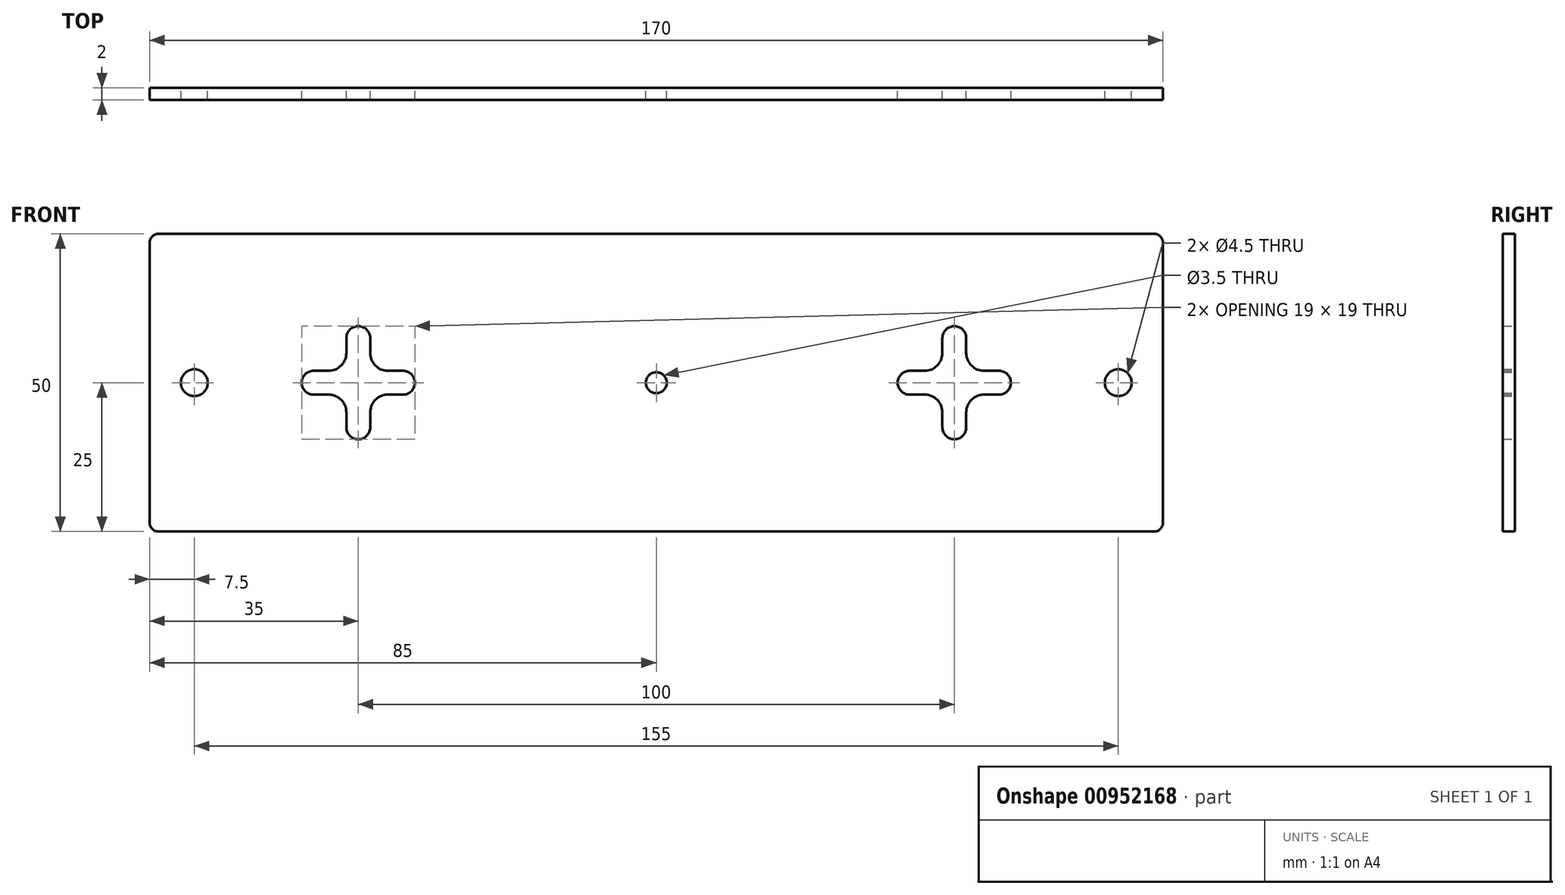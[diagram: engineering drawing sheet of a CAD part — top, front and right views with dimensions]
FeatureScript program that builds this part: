
annotation { "Feature Type Name" : "Feature", "Feature Type Description" : "" }
export const myFeature = defineFeature(function(context is Context, id is Id, definition is map)
    precondition{}
    {
        {
            var Q0;
            Q0=qCreatedBy(makeId("Front.planeOp"),FACE);
            var sketch = newSketch(context, id + "F0", { "sketchPlane" : qUnion([Q0])});
            skLineSegment(sketch, "E0.bottom", {"start": v(0, 0) * mm, "end": v(170, 0) * mm});
            skLineSegment(sketch, "E0.top", {"start": v(0, 50) * mm, "end": v(170, 50) * mm});
            skLineSegment(sketch, "E0.left", {"start": v(0, 0) * mm, "end": v(0, 50) * mm});
            skLineSegment(sketch, "E0.right", {"start": v(170, 0) * mm, "end": v(170, 50) * mm});
            skCircle(sketch, "E1", {"center": v(7.5, 25) * mm, "radius": 2.25 * mm});
            skCircle(sketch, "E2", {"center": v(162.5, 25) * mm, "radius": 2.25 * mm});
            skCircle(sketch, "E3", {"center": v(85, 25) * mm, "radius": 1.75 * mm});
            skLineSegment(sketch, "E4", {"start": v(35, 32.5) * mm, "end": v(35, 17.5) * mm});
            skLineSegment(sketch, "E5", {"start": v(27.5, 25) * mm, "end": v(42.5, 25) * mm});
            skArc(sketch, "E6.0.startCap", {"start": v(33, 32.5) * mm, "mid": v(35, 34.5) * mm, "end": v(37, 32.5) * mm});
            skArc(sketch, "E6.0.endCap", {"start": v(37, 17.5) * mm, "mid": v(35, 15.5) * mm, "end": v(33, 17.5) * mm});
            skLineSegment(sketch, "E6.0.left", {"start": v(37, 32.5) * mm, "end": v(37, 17.5) * mm});
            skLineSegment(sketch, "E6.0.right", {"start": v(33, 32.5) * mm, "end": v(33, 17.5) * mm});
            skArc(sketch, "E6.1.startCap", {"start": v(27.5, 23) * mm, "mid": v(25.5, 25) * mm, "end": v(27.5, 27) * mm});
            skArc(sketch, "E6.1.endCap", {"start": v(42.5, 27) * mm, "mid": v(44.5, 25) * mm, "end": v(42.5, 23) * mm});
            skLineSegment(sketch, "E6.1.left", {"start": v(27.5, 27) * mm, "end": v(42.5, 27) * mm});
            skLineSegment(sketch, "E6.1.right", {"start": v(27.5, 23) * mm, "end": v(42.5, 23) * mm});
            skLineSegment(sketch, "E7.1.0.0", {"start": v(127.5, 27) * mm, "end": v(142.5, 27) * mm});
            skLineSegment(sketch, "E7.1.0.1", {"start": v(135, 32.5) * mm, "end": v(135, 17.5) * mm});
            skLineSegment(sketch, "E7.1.0.2", {"start": v(133, 32.5) * mm, "end": v(133, 17.5) * mm});
            skLineSegment(sketch, "E7.1.0.3", {"start": v(137, 32.5) * mm, "end": v(137, 17.5) * mm});
            skArc(sketch, "E7.1.0.4", {"start": v(137, 17.5) * mm, "mid": v(135, 15.5) * mm, "end": v(133, 17.5) * mm});
            skArc(sketch, "E7.1.0.5", {"start": v(142.5, 27) * mm, "mid": v(144.5, 25) * mm, "end": v(142.5, 23) * mm});
            skLineSegment(sketch, "E7.1.0.6", {"start": v(127.5, 23) * mm, "end": v(142.5, 23) * mm});
            skArc(sketch, "E7.1.0.7", {"start": v(133, 32.5) * mm, "mid": v(135, 34.5) * mm, "end": v(137, 32.5) * mm});
            skArc(sketch, "E7.1.0.8", {"start": v(127.5, 23) * mm, "mid": v(125.5, 25) * mm, "end": v(127.5, 27) * mm});
            skLineSegment(sketch, "E7.1.0.9", {"start": v(127.5, 25) * mm, "end": v(142.5, 25) * mm});
            skLineSegment(sketch, "E7.direction1", {"start": v(33, 17.5) * mm, "end": v(133, 17.5) * mm, "construction": true});
            skSolve(sketch);
        }
        {
            var Q0;
            {var subQ1=sQuery(id+"F0.wireOp",EDGE,"E0.top");Q0=makeQuery(id+"F0.imprint","IMPRINT",FACE,{"disambiguationData":[TD([[makeQuery(id+"F0.imprint","IMPRINT",EDGE,{"derivedFrom":subQ1}),-1.0]])]});}
            var Q1;
            {var subQ8=sQuery(id+"F0.wireOp",EDGE,"2fdba3b7-9a52-4864-9b49-22906f5ad9b7.0");Q1=makeQuery(id+"F0.imprint","IMPRINT",FACE,{"disambiguationData":[TD([[makeQuery(id+"F0.imprint","IMPRINT",EDGE,{"derivedFrom":subQ8}),-1.0]])]});}
            var Q2;
            {var subQ5=sQuery(id+"F0.wireOp",EDGE,"64e2a2b8-9ee0-4563-ae59-12d8a678591b.0");Q2=makeQuery(id+"F0.imprint","IMPRINT",FACE,{"disambiguationData":[TD([[makeQuery(id+"F0.imprint","IMPRINT",EDGE,{"derivedFrom":subQ5}),1.0]])]});}
            var Q3;
            {var subQ1=sQuery(id+"F0.wireOp",EDGE,"E0.bottom");Q3=makeQuery(id+"F0.imprint","IMPRINT",FACE,{"disambiguationData":[TD([[makeQuery(id+"F0.imprint","IMPRINT",EDGE,{"derivedFrom":subQ1}),1.0]])]});}
            extrude(context, id + "F1", {"entities" : qUnion([Q0, Q1, Q2, Q3]), "depth" : 2 * mm, "offsetDistance" : 25 * mm});
        }
        {
            var Q0;
            Q0=makeQuery(id+"F1.opExtrude","SWEPT_EDGE",EDGE,{"disambiguationData":[OSD([sQuery(id+"F0.wireOp",EDGE,"E6.0.right"),sQuery(id+"F0.wireOp",EDGE,"E6.1.left")])]});
            var Q1;
            Q1=makeQuery(id+"F1.opExtrude","SWEPT_EDGE",EDGE,{"disambiguationData":[OSD([sQuery(id+"F0.wireOp",EDGE,"E6.0.left"),sQuery(id+"F0.wireOp",EDGE,"E6.1.left")])]});
            var Q2;
            Q2=makeQuery(id+"F1.opExtrude","SWEPT_EDGE",EDGE,{"disambiguationData":[OSD([sQuery(id+"F0.wireOp",EDGE,"E6.0.left"),sQuery(id+"F0.wireOp",EDGE,"E6.1.right")])]});
            var Q3;
            Q3=makeQuery(id+"F1.opExtrude","SWEPT_EDGE",EDGE,{"disambiguationData":[OSD([sQuery(id+"F0.wireOp",EDGE,"E6.0.right"),sQuery(id+"F0.wireOp",EDGE,"E6.1.right")])]});
            var Q4;
            Q4=makeQuery(id+"F1.opExtrude","SWEPT_EDGE",EDGE,{"disambiguationData":[OSD([sQuery(id+"F0.wireOp",EDGE,"E7.1.0.0"),sQuery(id+"F0.wireOp",EDGE,"E7.1.0.2")])]});
            var Q5;
            Q5=makeQuery(id+"F1.opExtrude","SWEPT_EDGE",EDGE,{"disambiguationData":[OSD([sQuery(id+"F0.wireOp",EDGE,"E7.1.0.2"),sQuery(id+"F0.wireOp",EDGE,"E7.1.0.6")])]});
            var Q6;
            Q6=makeQuery(id+"F1.opExtrude","SWEPT_EDGE",EDGE,{"disambiguationData":[OSD([sQuery(id+"F0.wireOp",EDGE,"E7.1.0.0"),sQuery(id+"F0.wireOp",EDGE,"E7.1.0.3")])]});
            var Q7;
            Q7=makeQuery(id+"F1.opExtrude","SWEPT_EDGE",EDGE,{"disambiguationData":[OSD([sQuery(id+"F0.wireOp",EDGE,"E7.1.0.3"),sQuery(id+"F0.wireOp",EDGE,"E7.1.0.6")])]});
            fillet(context, id + "F2", {"entities" : qUnion([Q0, Q1, Q2, Q3, Q4, Q5, Q6, Q7]), "radius" : 3 * mm, "tangentPropagation" : true, "allowEdgeOverflow" : false});
        }
        {
            var Q0;
            Q0=makeQuery(id+"F1.opExtrude","SWEPT_EDGE",EDGE,{"disambiguationData":[OSD([sQuery(id+"F0.wireOp",EDGE,"E0.top"),sQuery(id+"F0.wireOp",EDGE,"E0.left")])]});
            var Q1;
            Q1=makeQuery(id+"F1.opExtrude","SWEPT_EDGE",EDGE,{"disambiguationData":[OSD([sQuery(id+"F0.wireOp",EDGE,"E0.bottom"),sQuery(id+"F0.wireOp",EDGE,"E0.left")])]});
            var Q2;
            Q2=makeQuery(id+"F1.opExtrude","SWEPT_EDGE",EDGE,{"disambiguationData":[OSD([sQuery(id+"F0.wireOp",EDGE,"E0.top"),sQuery(id+"F0.wireOp",EDGE,"E0.right")])]});
            var Q3;
            Q3=makeQuery(id+"F1.opExtrude","SWEPT_EDGE",EDGE,{"disambiguationData":[OSD([sQuery(id+"F0.wireOp",EDGE,"E0.bottom"),sQuery(id+"F0.wireOp",EDGE,"E0.right")])]});
            fillet(context, id + "F3", {"entities" : qUnion([Q0, Q1, Q2, Q3]), "radius" : 1.5 * mm, "tangentPropagation" : true, "allowEdgeOverflow" : false});
        }
    });
